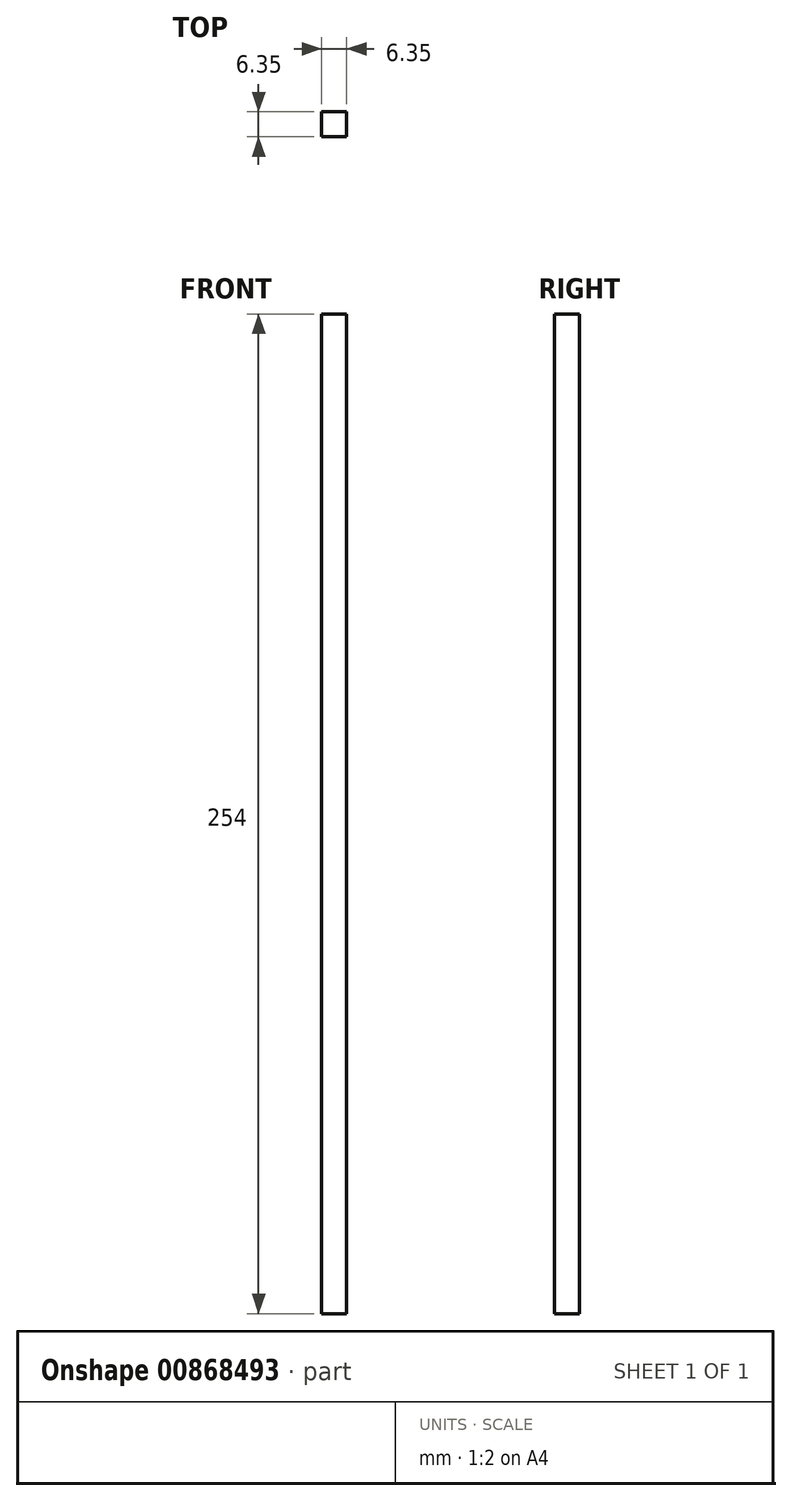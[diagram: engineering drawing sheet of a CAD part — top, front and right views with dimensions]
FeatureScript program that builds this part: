
annotation { "Feature Type Name" : "Feature", "Feature Type Description" : "" }
export const myFeature = defineFeature(function(context is Context, id is Id, definition is map)
    precondition{}
    {
        {
            var Q0;
            Q0=qCreatedBy(makeId("Top.planeOp"),FACE);
            var sketch = newSketch(context, id + "F0", { "sketchPlane" : qUnion([Q0])});
            skLineSegment(sketch, "E0.bottom", {"start": v(-36.15, 25.97) * mm, "end": v(-29.8, 25.97) * mm});
            skLineSegment(sketch, "E0.top", {"start": v(-36.15, 19.62) * mm, "end": v(-29.8, 19.62) * mm});
            skLineSegment(sketch, "E0.left", {"start": v(-36.15, 25.97) * mm, "end": v(-36.15, 19.62) * mm});
            skLineSegment(sketch, "E0.right", {"start": v(-29.8, 25.97) * mm, "end": v(-29.8, 19.62) * mm});
            skSolve(sketch);
        }
        {
            var Q0;
            Q0 = qSketchRegion(id + "F0", true);
            extrude(context, id + "F1", {"entities" : qUnion([Q0]), "depth" : 254 * mm, "offsetDistance" : 25.4 * mm});
        }
    });
